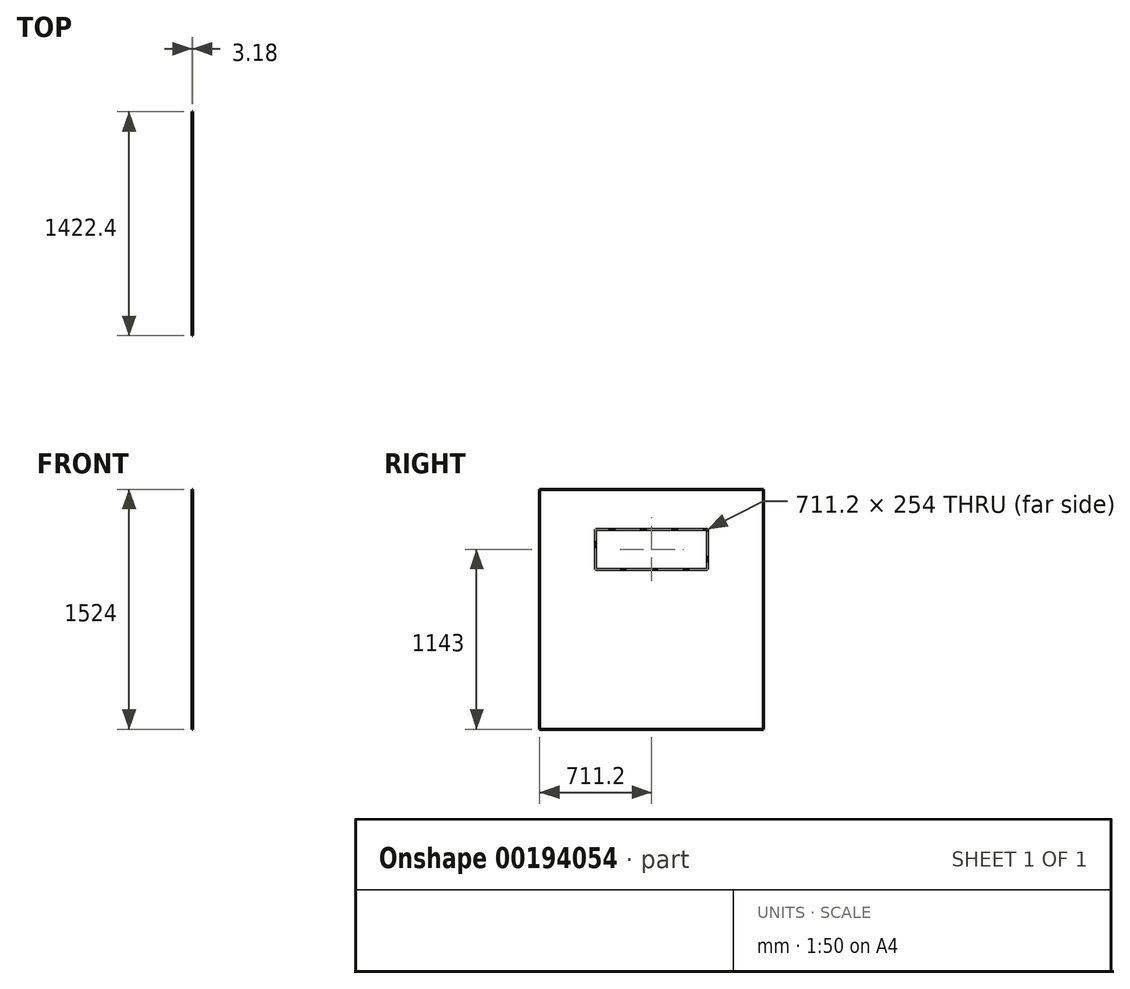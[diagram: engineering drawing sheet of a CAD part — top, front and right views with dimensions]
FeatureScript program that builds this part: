
annotation { "Feature Type Name" : "Feature", "Feature Type Description" : "" }
export const myFeature = defineFeature(function(context is Context, id is Id, definition is map)
    precondition{}
    {
        {
            var Q0;
            Q0=qCreatedBy(makeId("Right.planeOp"),FACE);
            var sketch = newSketch(context, id + "F0", { "sketchPlane" : qUnion([Q0])});
            skLineSegment(sketch, "E0.bottom", {"start": v(-711.2, 762) * mm, "end": v(711.2, 762) * mm});
            skLineSegment(sketch, "E0.top", {"start": v(-711.2, -762) * mm, "end": v(711.2, -762) * mm});
            skLineSegment(sketch, "E0.left", {"start": v(-711.2, 762) * mm, "end": v(-711.2, -762) * mm});
            skLineSegment(sketch, "E0.right", {"start": v(711.2, 762) * mm, "end": v(711.2, -762) * mm});
            skPoint(sketch, "E0.middle", {"position": v(0, 0) * mm});
            skSolve(sketch);
        }
        {
            var Q0;
            Q0=makeQuery(id+"F0.imprint","IMPRINT",FACE,{"disambiguationData":[TD([[makeQuery(id+"F0.imprint","IMPRINT",EDGE,{"derivedFrom":sQuery(id+"F0.wireOp",EDGE,"E0.bottom")}),-1.0]])]});
            extrude(context, id + "F1", {"entities" : qUnion([Q0]), "depth" : 3.17 * mm});
        }
        {
            var Q0;
            Q0=makeQuery(id+"F1.opExtrude","CAP_FACE",FACE,{"disambiguationData":[OSD([sQuery(id+"F0.wireOp",EDGE,"E0.bottom"),sQuery(id+"F0.wireOp",EDGE,"E0.top"),sQuery(id+"F0.wireOp",EDGE,"E0.left"),sQuery(id+"F0.wireOp",EDGE,"E0.right")])],"isStart":false});
            var sketch = newSketch(context, id + "F2", { "sketchPlane" : qUnion([Q0])});
            skLineSegment(sketch, "E1", {"start": v(0, 0) * mm, "end": v(0, 508) * mm, "construction": true});
            skPoint(sketch, "E1.endSnap0", {"position": v(0, 762) * mm});
            skLineSegment(sketch, "E2", {"start": v(0, 508) * mm, "end": v(-355.6, 508) * mm, "construction": true});
            skLineSegment(sketch, "E3", {"start": v(0, 508) * mm, "end": v(355.6, 508) * mm, "construction": true});
            skLineSegment(sketch, "E4", {"start": v(355.6, 508) * mm, "end": v(355.6, 254) * mm, "construction": true});
            skLineSegment(sketch, "E5", {"start": v(355.6, 254) * mm, "end": v(-355.6, 254) * mm, "construction": true});
            skLineSegment(sketch, "E6", {"start": v(-355.6, 254) * mm, "end": v(-355.6, 508) * mm, "construction": true});
            skLineSegment(sketch, "E7.bottom", {"start": v(355.6, 508) * mm, "end": v(-355.6, 508) * mm});
            skLineSegment(sketch, "E7.top", {"start": v(355.6, 254) * mm, "end": v(-355.6, 254) * mm});
            skLineSegment(sketch, "E7.left", {"start": v(355.6, 508) * mm, "end": v(355.6, 254) * mm});
            skLineSegment(sketch, "E7.right", {"start": v(-355.6, 508) * mm, "end": v(-355.6, 254) * mm});
            skSolve(sketch);
        }
        {
            var Q0;
            Q0=makeQuery(id+"F2.imprint","IMPRINT",FACE,{"disambiguationData":[TD([[makeQuery(id+"F2.imprint","IMPRINT",EDGE,{"derivedFrom":sQuery(id+"F2.wireOp",EDGE,"E7.bottom")}),1.0]])]});
            extrude(context, id + "F3", {"entities" : qUnion([Q0]), "operationType" : NewBodyOperationType.REMOVE, "endBound" : BoundingType.THROUGH_ALL, "oppositeDirection" : true, "depth" : 25.4 * mm});
        }
    });
